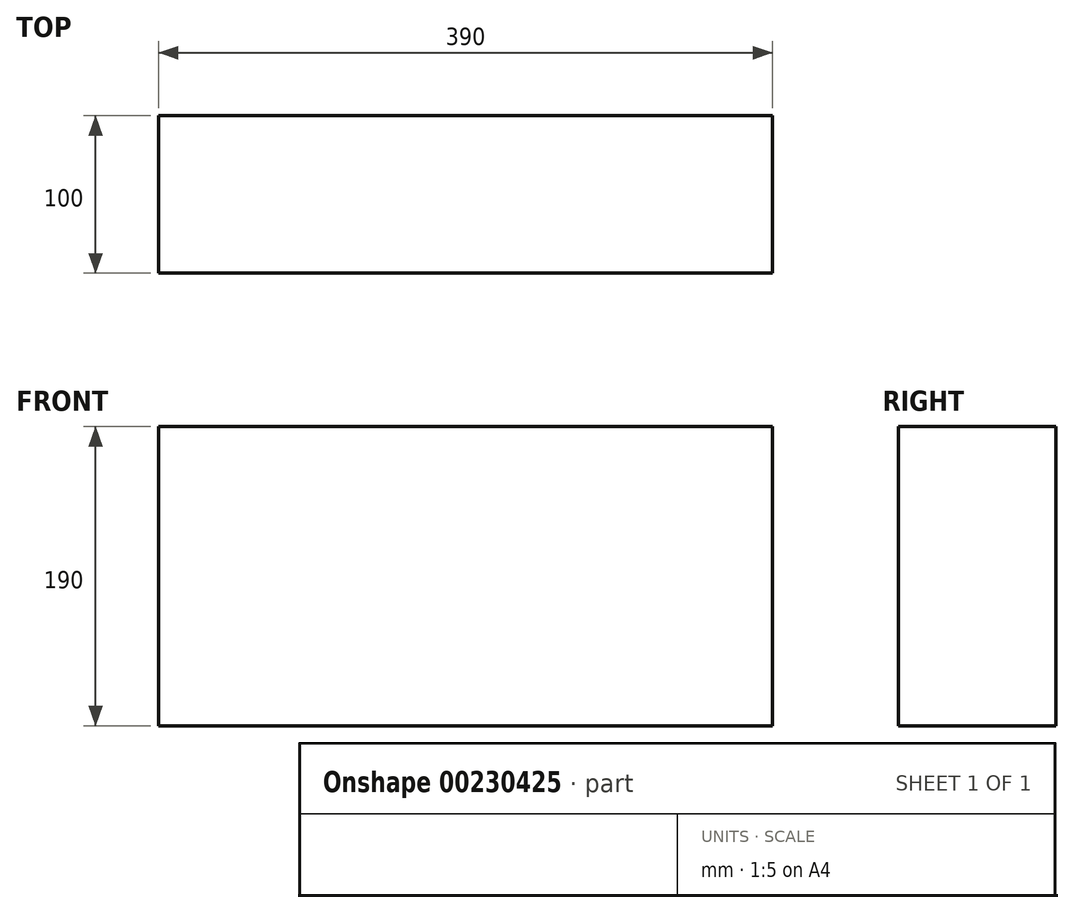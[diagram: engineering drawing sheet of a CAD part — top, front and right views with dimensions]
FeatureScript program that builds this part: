
annotation { "Feature Type Name" : "Feature", "Feature Type Description" : "" }
export const myFeature = defineFeature(function(context is Context, id is Id, definition is map)
    precondition{}
    {
        {
            var Q0;
            Q0=qCreatedBy(makeId("Top.planeOp"),FACE);
            var sketch = newSketch(context, id + "F0", { "sketchPlane" : qUnion([Q0])});
            skLineSegment(sketch, "E0.bottom", {"start": v(-196.99, -33.82) * mm, "end": v(193.01, -33.82) * mm});
            skLineSegment(sketch, "E0.top", {"start": v(-196.99, -133.82) * mm, "end": v(193.01, -133.82) * mm});
            skLineSegment(sketch, "E0.left", {"start": v(-196.99, -33.82) * mm, "end": v(-196.99, -133.82) * mm});
            skLineSegment(sketch, "E0.right", {"start": v(193.01, -33.82) * mm, "end": v(193.01, -133.82) * mm});
            skSolve(sketch);
        }
        {
            var Q0;
            Q0 = qSketchRegion(id + "F0", true);
            extrude(context, id + "F1", {"entities" : qUnion([Q0]), "depth" : 190 * mm});
        }
    });
